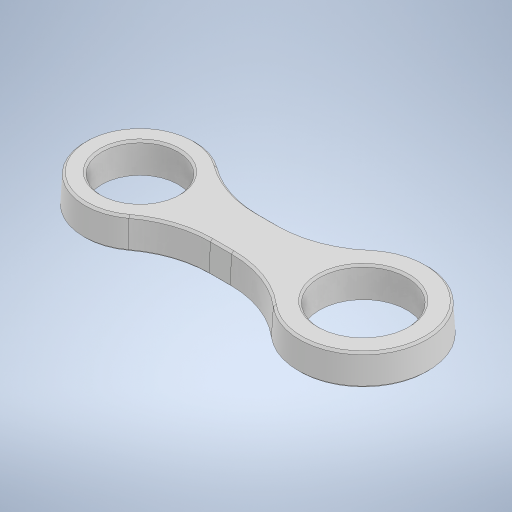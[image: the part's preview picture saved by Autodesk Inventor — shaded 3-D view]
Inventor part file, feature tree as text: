
AUTODESK INVENTOR PART (.ipt)
format: ipt  version: 2023 (Build 270158000, 158)  size: 314,880 bytes
history: native  units: in
note: dims shown in document units (in); Inventor stores cm internally (conversion verified against a paired STEP export)
features: chamfer x2, extrude x1, fillet x1, draft x1, sketch x1
ambient origin geometry x8: Origin, YZ Plane, XZ Plane, XY Plane, X Axis, Y Axis, Z Axis, Center Point
bodies: Body1 (feature_tree)
feature tree (6):
  extrude  "Extrusion2"  Depth=1.0in
  fillet  "Fillet3"  Radius=1.3in
  draft  "FaceDraft2"
  chamfer  "Chamfer1"  Distance=0.76in
  chamfer  "Chamfer2"  Distance=1.125in
  sketch  "Sketch1"  dims[d15=0.872in d17=0.5in d18=1.3in d19=0.76in d20=1.125in d21=2.225in d22=0.3in d23=0.0in d27=1.0in d28=0.0206in d29=0.02in d30=0.125in d31=45.0deg d32=0.02in d33=0.125in d34=45.0deg d3=0.5in d4=0.0344in d5=0.5in d6=0.0344in]
